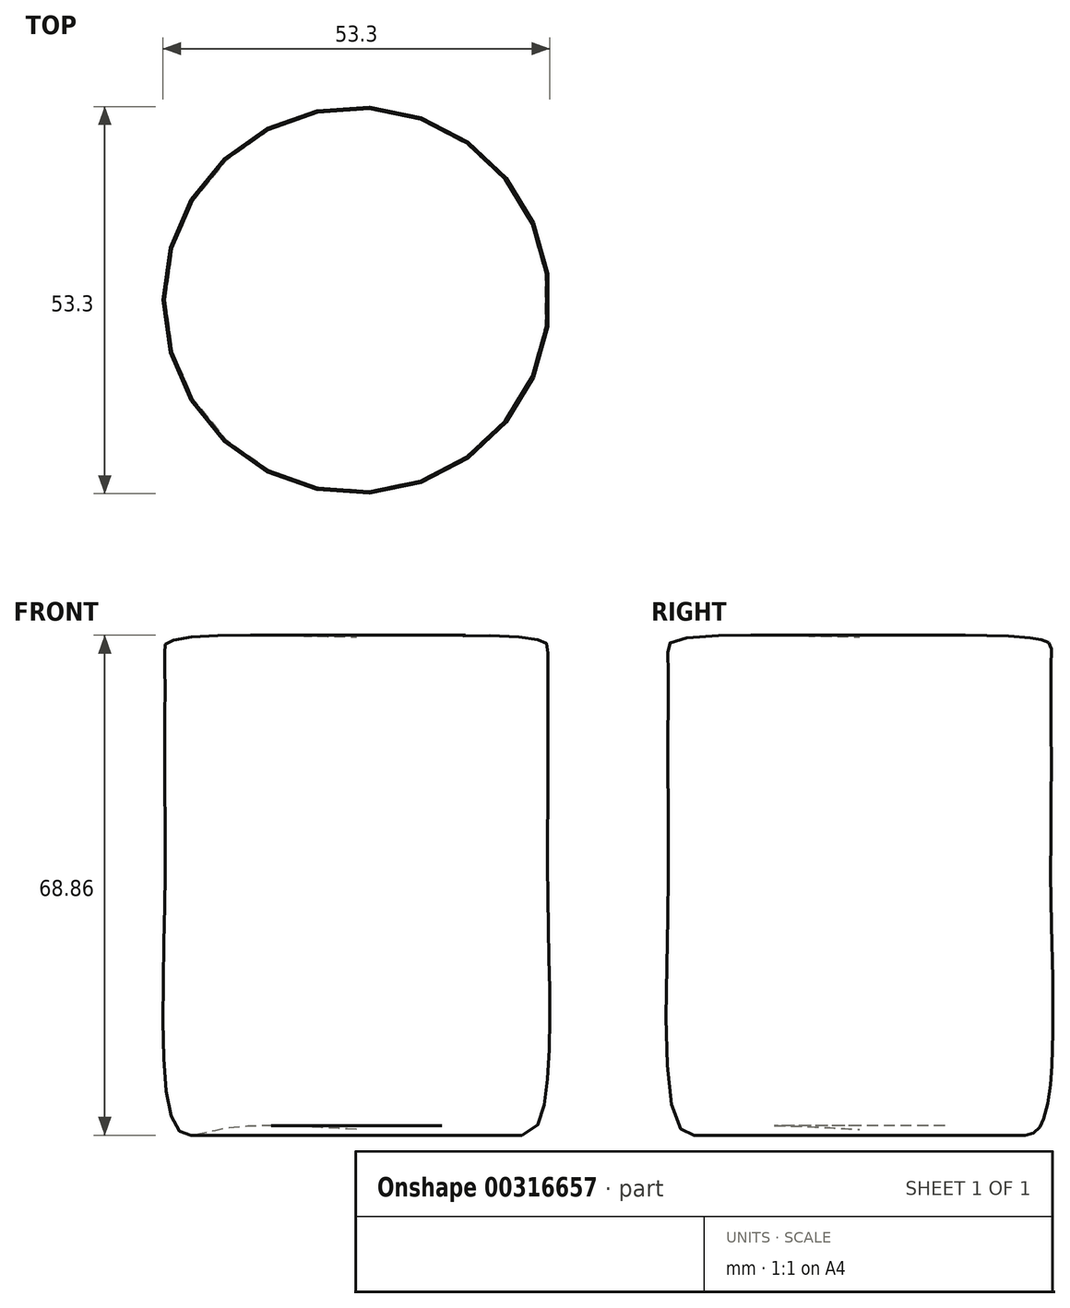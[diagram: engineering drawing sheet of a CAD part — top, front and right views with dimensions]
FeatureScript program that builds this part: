
annotation { "Feature Type Name" : "Feature", "Feature Type Description" : "" }
export const myFeature = defineFeature(function(context is Context, id is Id, definition is map)
    precondition{}
    {
        {
            var Q0;
            Q0=qCreatedBy(makeId("Front.planeOp"),FACE);
            var sketch = newSketch(context, id + "F0", { "sketchPlane" : qUnion([Q0])});
            skLineSegment(sketch, "E0", {"start": v(0, 0) * mm, "end": v(0, 79.55) * mm});
            skFitSpline(sketch, "E1", {"points": [v(0, 0) * mm, v(-18.83, 0) * mm, v(-24.57, 0) * mm, v(-26.4, 29.27) * mm, v(-26.4, 50.85) * mm, v(-26.4, 65.55) * mm, v(-25.94, 67.15) * mm, v(0, 67.84) * mm], "startDerivative": vector(-131.66, 8.62) * mm, "endDerivative": vector(188.83, -4.57) * mm});
            skSolve(sketch);
        }
        {
            var Q0;
            {var subQ0=sQuery(id+"F0.wireOp",EDGE,"E1");Q0=makeQuery(id+"F0.imprint","IMPRINT",FACE,{"disambiguationData":[TD([[makeQuery(id+"F0.imprint","IMPRINT",EDGE,{"derivedFrom":subQ0}),-1.0]])]});}
            var Q1;
            Q1=sQuery(id+"F0.wireOp",EDGE,"E0");
            revolve(context, id + "F1", {"entities" : qUnion([Q0]), "axis" : qUnion([Q1]), "revolveType" : RevolveType.FULL});
        }
        {
            var Q0;
            Q0=qCreatedBy(makeId("Front.planeOp"),FACE);
            var sketch = newSketch(context, id + "F2", { "sketchPlane" : qUnion([Q0])});
            skFitSpline(sketch, "E2", {"points": [v(-27.1, 49.48) * mm, v(-32.14, 49.25) * mm, v(-40.64, 45.34) * mm, v(-45.92, 35.24) * mm, v(-46.6, 22.15) * mm, v(-40.64, 14.12) * mm, v(-29.39, 11.6) * mm, v(-26.86, 11.6) * mm], "startDerivative": vector(-42.3, 1.61) * mm, "endDerivative": vector(25.33, 1.18) * mm});
            skSolve(sketch);
        }
        {
            var Q0;
            Q0=sQuery(id+"F2.wireOp",EDGE,"E2");
            extrude(context, id + "F3", {"bodyType" : ToolBodyType.SURFACE, "surfaceEntities" : qUnion([Q0]), "depth" : 12.7 * mm});
        }
    });
